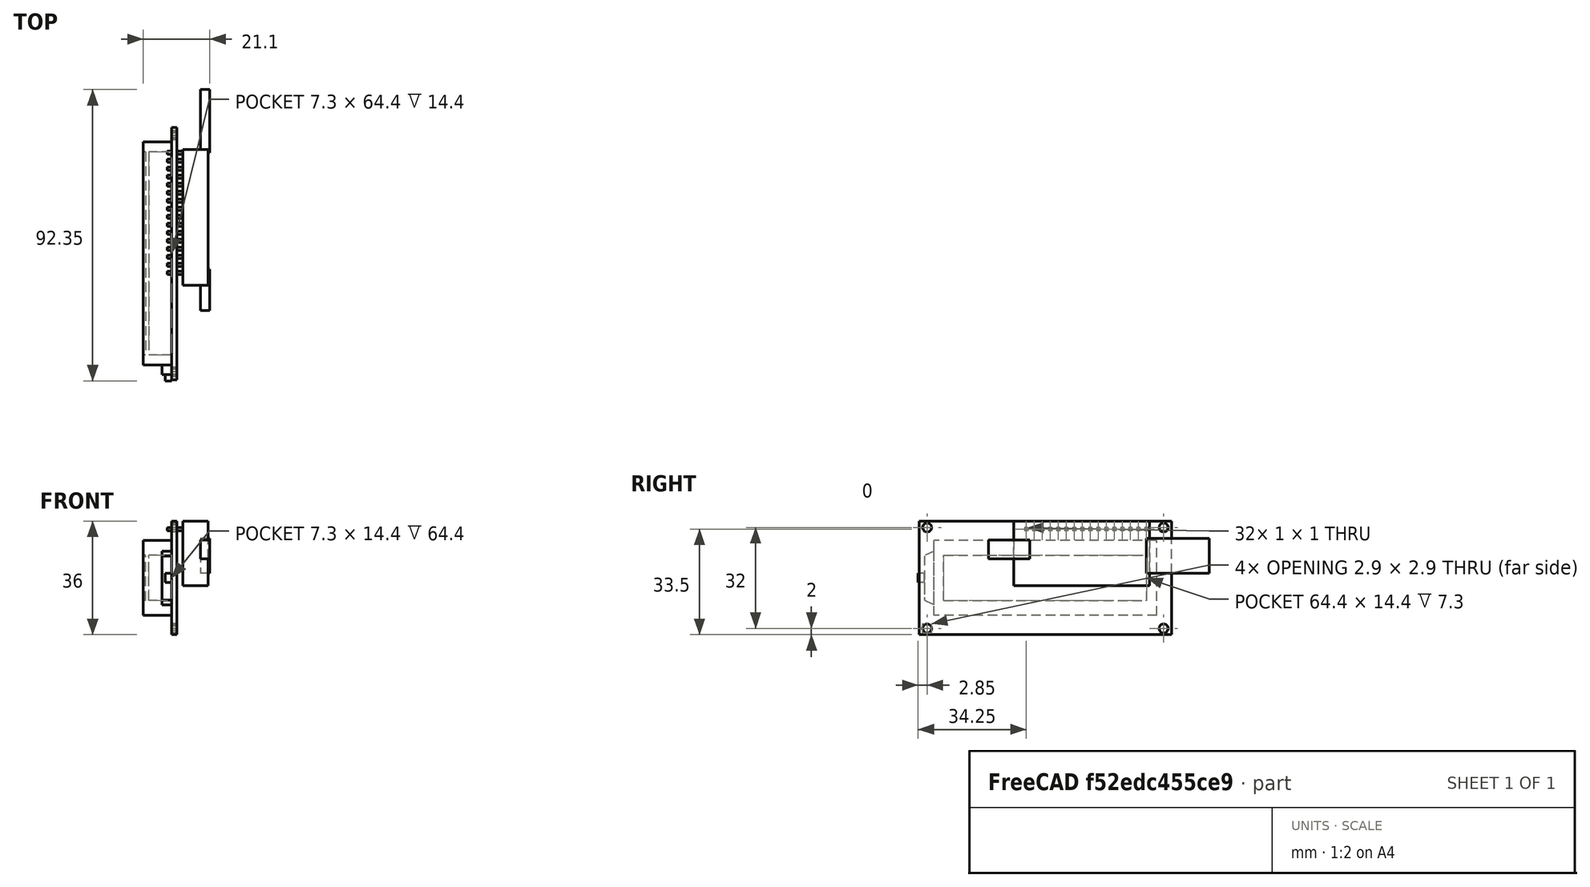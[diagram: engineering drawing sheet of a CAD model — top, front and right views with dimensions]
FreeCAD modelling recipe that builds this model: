
FCSTD DOCUMENT  (FreeCAD 0.16R6712 (Git))
Label: rssi_tracker
License: CC-BY 3.0
LicenseURL: http://creativecommons.org/licenses/by/3.0/
objects: Part::Box×24, Mesh::Feature×15, Part::Prism×4, App::DocumentObjectGroup×3, Part::MultiFuse×3, Part::Cut×2, Part::Fuse×1, Part::Feature×1, Part::FeaturePython×1, Part::Extrusion×1
note: 37 computed .brp shape members not serialized (recipe doc carries the construction recipe); baked Part::Feature solids carry a one-line shape summary decoded from their .brp

FEATURE [Mesh::Feature] top_case_base
  Placement = pos=(0,0,-8) rot=(0,0,1;0rad)
FEATURE [Mesh::Feature] top_case_pcb_cover
  Placement = pos=(0,0,17) rot=(1,0,0;3.14159rad)
FEATURE [Mesh::Feature] top_case_bracket  label="top_case_bracket_left"
  Placement = pos=(54,50,27.5) rot=(0,-1,0;1.5708rad)
FEATURE [Mesh::Feature] top_case_bracket001  label="top_case_bracket_right"
  Placement = pos=(-50,50,27.5) rot=(0,-1,0;1.5708rad)
FEATURE [Mesh::Feature] antenna_mount_bracket  label="antenna_mount_bracket_left"
  Placement = pos=(55,50,28) rot=(0.57735,-0.57735,0.57735;4.18879rad)
FEATURE [Mesh::Feature] antenna_mount_bracket001  label="antenna_mount_bracket_right"
  Placement = pos=(-59,50,28) rot=(0.57735,-0.57735,0.57735;4.18879rad)
FEATURE [Mesh::Feature] antenna_mount  label="antenna_mount_mount"
  Placement = pos=(0,50,30) rot=(0,0,-1;1.5708rad)
FEATURE [App::DocumentObjectGroup] Group  label="top_case"
  Group = -> [top_case_base,top_case_pcb_cover,top_case_bracket,top_case_bracket001]
FEATURE [App::DocumentObjectGroup] Group001  label="antenna_mount"
  Group = -> [antenna_mount_bracket,antenna_mount_bracket001,antenna_mount]
FEATURE [Mesh::Feature] lower_bottom_case
  Placement = pos=(0,12,-71) rot=(0,0,1;0rad)
FEATURE [Mesh::Feature] upper_bottom_case
  Placement = pos=(0,12,-23) rot=(1,0,0;3.14159rad)
FEATURE [Mesh::Feature] bottom_case_bearing_mount
  Placement = pos=(0,12,-23) rot=(0,0,1;0rad)
FEATURE [App::DocumentObjectGroup] Group002  label="bottom_case"
  Group = -> [lower_bottom_case,upper_bottom_case,bottom_case_bearing_mount]
FEATURE [Mesh::Feature] ballrace
  Placement = pos=(0,12,-11.5) rot=(0,0,1;0rad)
FEATURE [Mesh::Feature] bottom_case_bearing_retaining_disc
  Placement = pos=(0,12,-8) rot=(0,0,1;0rad)
FEATURE [Mesh::Feature] large_gear
  Placement = pos=(0,12,-18) rot=(0,0,1;0rad)
FEATURE [Mesh::Feature] servo
  Placement = pos=(-25.2,48,-8.5) rot=(0,0,1;3.14159rad)
FEATURE [Mesh::Feature] servo_gear
  Placement = pos=(-25,48,-10) rot=(1,0,0;3.14159rad)
FEATURE [Part::Box] cube
  Height = 1.6
  Length = 80
  Width = 36
FEATURE [Part::Prism] prism
  Circumradius = 1.45
  Height = 10
  Placement = pos=(2.5,2,-5) rot=(0,0,1;0rad)
  Polygon = 12
FEATURE [Part::Prism] prism001
  Circumradius = 1.45
  Height = 10
  Placement = pos=(2.5,34,-5) rot=(0,0,1;0rad)
  Polygon = 12
FEATURE [Part::Prism] prism002
  Circumradius = 1.45
  Height = 10
  Placement = pos=(77.5,2,-5) rot=(0,0,1;0rad)
  Polygon = 12
FEATURE [Part::Prism] prism003
  Circumradius = 1.45
  Height = 10
  Placement = pos=(77.5,34,-5) rot=(0,0,1;0rad)
  Polygon = 12
FEATURE [Part::MultiFuse] Group003
  Shapes = -> [prism,prism001,prism002,prism003]
FEATURE [Part::Cut] difference
  Base = -> cube
  Tool = -> Group003
FEATURE [Part::Box] cube001
  Height = 9
  Length = 70.7
  Width = 23.8
FEATURE [Part::Box] cube002
  Height = 20
  Length = 64.4
  Placement = pos=(3.15,4.7,-10) rot=(0,0,1;0rad)
  Width = 14.4
FEATURE [Part::Cut] difference001
  Base = -> cube001
  Tool = -> cube002
FEATURE [Part::Box] cube003
  Height = 1
  Length = 64.4
  Placement = pos=(3.15,4.7,7.3) rot=(0,0,1;0rad)
  Width = 14.4
FEATURE [Part::Fuse] Matrix_Union
  Base = -> difference001
  Placement = pos=(4.65,6.1,1.6) rot=(0,0,1;0rad)
  Tool = -> cube003
FEATURE [Part::Feature] polygon
  shape: bbox 3 x 17 x 2e-07 mm, 1 faces, 0 solids (baked)
FEATURE [Part::FeaturePython] RefineLinearExtrude  # WARN: FeaturePython — macro-defined, semantics opaque (R4)
  Base = -> polygon
FEATURE [Part::Extrusion] LinearExtrude
  Base = -> RefineLinearExtrude
  Dir = (0,0,3)
  Placement = pos=(75.35,18,1.6) rot=(0,0,1;0rad)
  Solid = true
FEATURE [Part::Box] cube004
  Height = 2
  Length = 2
  Placement = pos=(78.35,16.5,1.6) rot=(0,0,1;0rad)
  Width = 3
FEATURE [Part::Box] cube005 .. cube020  x16 (patterned run collapsed; names and placements below)
  Height = 13
  Length = 1
  Width = 1
  placements: 16 in arithmetic series — first pos=(7.5,33,-10) rot=(0,0,1;0rad), step (2.54,0,0), last pos=(45.6,33,-10) rot=(0,0,1;0rad)
FEATURE [Part::MultiFuse] Group004
  Shapes = -> [cube005,cube006,cube007,cube008,cube009,cube010,cube011,cube012,cube013,cube014,cube015,cube016,cube017,cube018,cube019,cube020]
FEATURE [Part::Box] cube021
  Height = 8
  Length = 43
  Placement = pos=(7,15.5,-10) rot=(0,0,1;0rad)
  Width = 20.5
FEATURE [Part::Box] cube022
  Height = 3
  Length = 20
  Placement = pos=(-12,19.5,-10.5) rot=(0,0,1;0rad)
  Width = 11
FEATURE [Part::Box] cube023
  Height = 3
  Length = 13
  Placement = pos=(45,24,-10.5) rot=(0,0,1;0rad)
  Width = 6
FEATURE [Part::MultiFuse] Group005
  Placement = pos=(-59,44.35,-65) rot=(0.57735,-0.57735,-0.57735;2.0944rad)
  Shapes = -> [difference,Matrix_Union,LinearExtrude,cube004,Group004,cube021,cube022,cube023]
